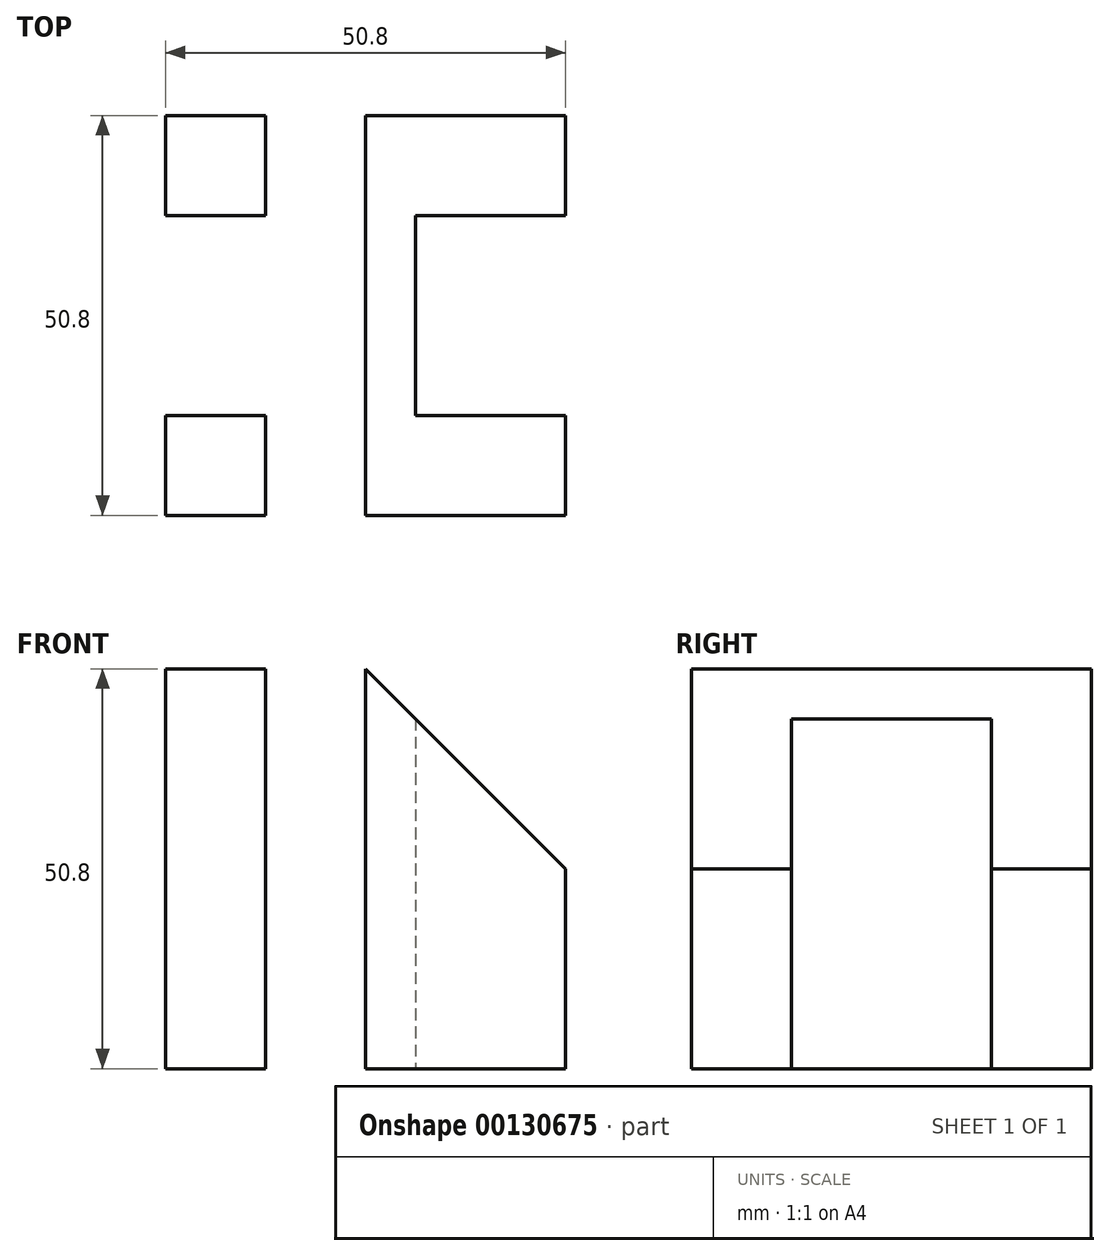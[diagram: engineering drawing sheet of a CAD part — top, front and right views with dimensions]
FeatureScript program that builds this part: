
annotation { "Feature Type Name" : "Feature", "Feature Type Description" : "" }
export const myFeature = defineFeature(function(context is Context, id is Id, definition is map)
    precondition{}
    {
        {
            var Q0;
            Q0=qCreatedBy(makeId("Top.planeOp"),FACE);
            var sketch = newSketch(context, id + "F0", { "sketchPlane" : qUnion([Q0])});
            skLineSegment(sketch, "E0.bottom", {"start": v(0, 0) * mm, "end": v(50.8, 0) * mm});
            skLineSegment(sketch, "E0.top", {"start": v(0, 50.8) * mm, "end": v(50.8, 50.8) * mm});
            skLineSegment(sketch, "E0.left", {"start": v(0, 0) * mm, "end": v(0, 50.8) * mm});
            skLineSegment(sketch, "E0.right", {"start": v(50.8, 0) * mm, "end": v(50.8, 50.8) * mm});
            skLineSegment(sketch, "E1.bottom", {"start": v(50.8, 38.1) * mm, "end": v(31.75, 38.1) * mm});
            skLineSegment(sketch, "E1.top", {"start": v(50.8, 12.7) * mm, "end": v(31.75, 12.7) * mm});
            skLineSegment(sketch, "E1.left", {"start": v(50.8, 38.1) * mm, "end": v(50.8, 12.7) * mm});
            skLineSegment(sketch, "E1.right", {"start": v(31.75, 38.1) * mm, "end": v(31.75, 12.7) * mm});
            skLineSegment(sketch, "E2.bottom", {"start": v(0, 50.8) * mm, "end": v(12.7, 50.8) * mm});
            skLineSegment(sketch, "E2.top", {"start": v(0, 38.1) * mm, "end": v(12.7, 38.1) * mm});
            skLineSegment(sketch, "E2.left", {"start": v(0, 50.8) * mm, "end": v(0, 38.1) * mm});
            skLineSegment(sketch, "E2.right", {"start": v(12.7, 50.8) * mm, "end": v(12.7, 38.1) * mm});
            skLineSegment(sketch, "E3.bottom", {"start": v(0, 0) * mm, "end": v(12.7, 0) * mm});
            skLineSegment(sketch, "E3.top", {"start": v(0, 12.7) * mm, "end": v(12.7, 12.7) * mm});
            skLineSegment(sketch, "E3.left", {"start": v(0, 0) * mm, "end": v(0, 12.7) * mm});
            skLineSegment(sketch, "E3.right", {"start": v(12.7, 0) * mm, "end": v(12.7, 12.7) * mm});
            skLineSegment(sketch, "E4", {"start": v(25.4, 50.8) * mm, "end": v(25.4, 0) * mm});
            skSolve(sketch);
        }
        {
            var Q0;
            {var subQ5=sQuery(id+"F0.wireOp",EDGE,"E1.top");Q0=makeQuery(id+"F0.imprint","IMPRINT",FACE,{"disambiguationData":[TD([[makeQuery(id+"F0.imprint","IMPRINT",EDGE,{"derivedFrom":subQ5}),1.0]])]});}
            var Q1;
            {var subQ5=sQuery(id+"F0.wireOp",EDGE,"E1.bottom");Q1=makeQuery(id+"F0.imprint","IMPRINT",FACE,{"disambiguationData":[TD([[makeQuery(id+"F0.imprint","IMPRINT",EDGE,{"derivedFrom":subQ5}),-1.0]])]});}
            var Q2;
            Q2=makeQuery(id+"F0.imprint","IMPRINT",FACE,{"disambiguationData":[TD([[makeQuery(id+"F0.imprint","IMPRINT",EDGE,{"derivedFrom":sQuery(id+"F0.wireOp",EDGE,"E0.left")}),-1.0]])]});
            extrude(context, id + "F1", {"entities" : qUnion([Q0, Q1, Q2]), "endBound" : BoundingType.SYMMETRIC, "depth" : 50.8 * mm});
        }
        {
            var Q0;
            Q0=makeQuery(id+"F1.opExtrude","SWEPT_FACE",FACE,{"disambiguationData":[OSD([sQuery(id+"F0.wireOp",EDGE,"E0.bottom")])]});
            var sketch = newSketch(context, id + "F2", { "sketchPlane" : qUnion([Q0])});
            skLineSegment(sketch, "E5", {"start": v(50.8, 0) * mm, "end": v(25.4, 25.4) * mm});
            skSolve(sketch);
        }
        {
            var Q0;
            Q0 = qSketchRegion(id + "F2", true);
            var Q1;
            {var subQ0=sQuery(id+"F2.wireOp",EDGE,"E5");Q1=makeQuery(id+"F2.imprint","IMPRINT",FACE,{"disambiguationData":[TD([[makeQuery(id+"F2.imprint","IMPRINT",EDGE,{"derivedFrom":subQ0}),-1.0]])]});}
            extrude(context, id + "F3", {"entities" : qUnion([Q0, Q1]), "operationType" : NewBodyOperationType.REMOVE, "endBound" : BoundingType.THROUGH_ALL, "oppositeDirection" : true, "depth" : 25.4 * mm});
        }
    });
